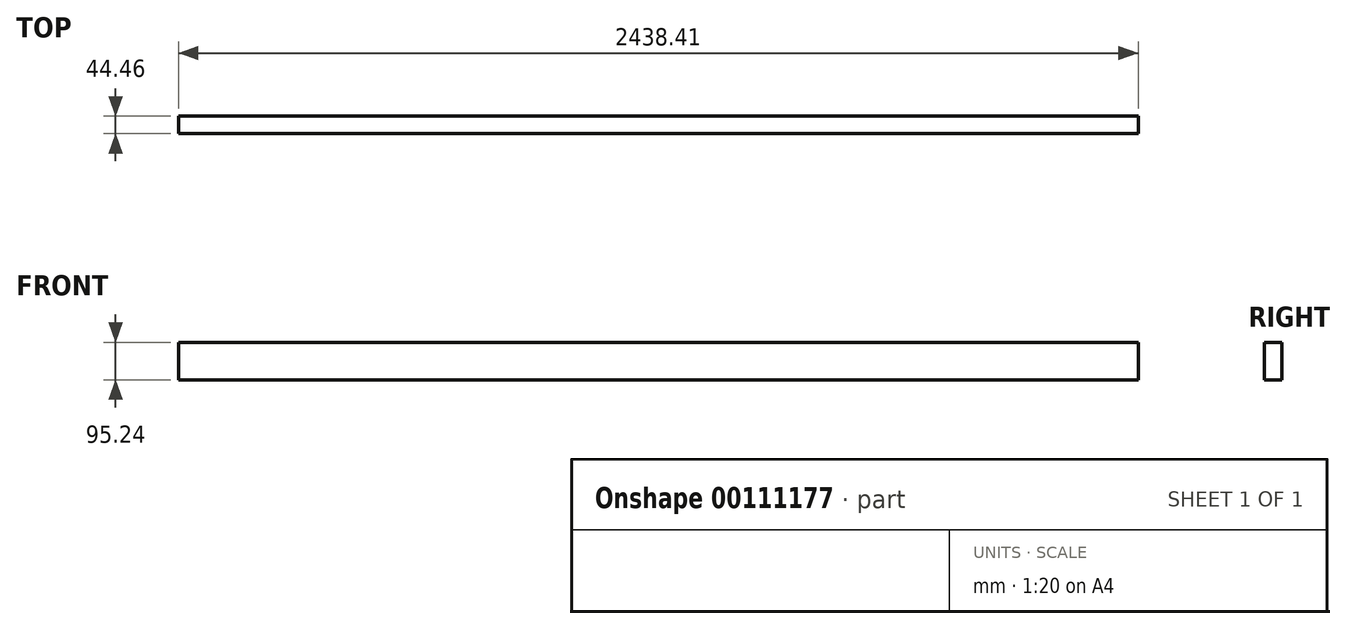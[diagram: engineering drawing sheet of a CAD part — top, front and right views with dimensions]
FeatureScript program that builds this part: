
annotation { "Feature Type Name" : "Feature", "Feature Type Description" : "" }
export const myFeature = defineFeature(function(context is Context, id is Id, definition is map)
    precondition{}
    {
        {
            var Q0;
            Q0=qCreatedBy(makeId("Front.planeOp"),FACE);
            var sketch = newSketch(context, id + "F0", { "sketchPlane" : qUnion([Q0])});
            skLineSegment(sketch, "E0.bottom", {"start": v(-1228.66, 57.77) * mm, "end": v(1228.66, 57.77) * mm});
            skLineSegment(sketch, "E0.top", {"start": v(-1228.66, -57.77) * mm, "end": v(1228.66, -57.77) * mm});
            skLineSegment(sketch, "E0.left", {"start": v(-1228.66, 57.77) * mm, "end": v(-1228.66, -57.77) * mm});
            skLineSegment(sketch, "E0.right", {"start": v(1228.66, 57.77) * mm, "end": v(1228.66, -57.77) * mm});
            skPoint(sketch, "E0.middle", {"position": v(0, 0) * mm});
            skSolve(sketch);
        }
        {
            var Q0;
            Q0=makeQuery(id+"F0.imprint","IMPRINT",FACE,{"disambiguationData":[TD([[makeQuery(id+"F0.imprint","IMPRINT",EDGE,{"derivedFrom":sQuery(id+"F0.wireOp",EDGE,"E0.bottom")}),-1.0]])]});
            extrude(context, id + "F1", {"entities" : qUnion([Q0]), "endBound" : BoundingType.SYMMETRIC, "depth" : 44.45 * mm});
        }
        {
            var Q0;
            Q0=makeQuery(id+"F1.opExtrude","SWEPT_FACE",FACE,{"disambiguationData":[OSD([sQuery(id+"F0.wireOp",EDGE,"E0.left")])]});
            extrude(context, id + "F2", {"entities" : qUnion([Q0]), "operationType" : NewBodyOperationType.ADD, "oppositeDirection" : true, "depth" : 192.94 * mm});
        }
        {
            var Q0;
            Q0=makeQuery(id+"F1.opExtrude","SWEPT_FACE",FACE,{"disambiguationData":[OSD([sQuery(id+"F0.wireOp",EDGE,"E0.left")])]});
            extrude(context, id + "F3", {"entities" : qUnion([Q0]), "operationType" : NewBodyOperationType.REMOVE, "oppositeDirection" : true, "depth" : 19.18 * mm});
        }
        {
            var Q0;
            Q0=makeQuery(id+"F3.boolean.opBoolean","COPY",FACE,{"derivedFrom":makeQuery(id+"F3.opExtrude","CAP_FACE",FACE,{"disambiguationData":[OSD([sQuery(id+"F0.wireOp",EDGE,"E0.left")])],"isStart":false})});
            extrude(context, id + "F4", {"entities" : qUnion([Q0]), "operationType" : NewBodyOperationType.ADD, "depth" : 0.27 * mm});
        }
        {
            var Q0;
            {var subQ0=sQuery(id+"F0.wireOp",EDGE,"E0.top");Q0=makeQuery(id+"F4.boolean.opBoolean","MERGE",FACE,{"derivedFrom":[makeQuery(id+"F1.opExtrude","SWEPT_FACE",FACE,{"disambiguationData":[OSD([subQ0])]}),makeQuery(id+"F4.opExtrude","SWEPT_FACE",FACE,{"disambiguationData":[OSD([subQ0,sQuery(id+"F0.wireOp",EDGE,"E0.left")])]})]});}
            extrude(context, id + "F5", {"entities" : qUnion([Q0]), "operationType" : NewBodyOperationType.REMOVE, "oppositeDirection" : true, "depth" : 12.7 * mm});
        }
        {
            var Q0;
            Q0=makeQuery(id+"F5.boolean.opBoolean","COPY",FACE,{"derivedFrom":makeQuery(id+"F5.opExtrude","CAP_FACE",FACE,{"disambiguationData":[OSD([sQuery(id+"F0.wireOp",EDGE,"E0.top"),sQuery(id+"F0.wireOp",EDGE,"E0.left")])],"isStart":false})});
            extrude(context, id + "F6", {"entities" : qUnion([Q0]), "operationType" : NewBodyOperationType.REMOVE, "oppositeDirection" : true, "depth" : 1.25 * mm});
        }
        {
            var Q0;
            Q0=makeQuery(id+"F6.boolean.opBoolean","COPY",FACE,{"derivedFrom":makeQuery(id+"F6.opExtrude","CAP_FACE",FACE,{"disambiguationData":[OSD([sQuery(id+"F0.wireOp",EDGE,"E0.top"),sQuery(id+"F0.wireOp",EDGE,"E0.left")])],"isStart":false})});
            extrude(context, id + "F7", {"entities" : qUnion([Q0]), "operationType" : NewBodyOperationType.REMOVE, "oppositeDirection" : true, "depth" : 25.4 * mm});
        }
        {
            var Q0;
            Q0=makeQuery(id+"F7.boolean.opBoolean","COPY",FACE,{"derivedFrom":makeQuery(id+"F7.opExtrude","CAP_FACE",FACE,{"disambiguationData":[OSD([sQuery(id+"F0.wireOp",EDGE,"E0.top"),sQuery(id+"F0.wireOp",EDGE,"E0.left")])],"isStart":false})});
            extrude(context, id + "F8", {"entities" : qUnion([Q0]), "operationType" : NewBodyOperationType.ADD, "depth" : 19.05 * mm});
        }
    });
